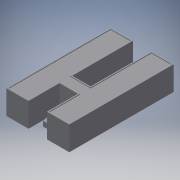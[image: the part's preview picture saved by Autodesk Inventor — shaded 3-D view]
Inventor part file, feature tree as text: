
AUTODESK INVENTOR PART (.ipt)
format: ipt  version: 2018.3 (Build 223284000, 284)  size: 178,688 bytes
history: native  units: mm
features: extrude x6, sketch x6
ambient origin geometry x8: Origin, YZ Plane, XZ Plane, XY Plane, X Axis, Y Axis, Z Axis, Center Point
bodies: Solid1 (feature_tree)
feature tree (12):
  extrude  "Extrusion1"  Depth=19.2mm
  extrude  "Extrusion2"  Depth=15.87mm
  extrude  "Extrusion3"  Depth=26.67mm
  extrude  "Extrusion4"  Depth=6.9mm
  extrude  "Extrusion5"  Depth=27.15mm TaperAngle=0.0deg
  extrude  "Extrusion6"  Depth=0.62mm
  sketch  "Sketch1"  dims[d0=90.0mm d1=19.2mm]
  sketch  "Sketch2"  dims[d2=52.35mm d3=15.87mm]
  sketch  "Sketch3"  dims[d4=19.2mm d5=26.67mm]
  sketch  "Sketch4"  dims[d6=20.67mm d7=0.0mm d8=6.9mm]
  sketch  "Sketch5"  dims[d9=4.29mm d10=27.15mm d11=0.0mm]
  sketch  "Sketch6"  dims[d12=24.88mm d13=14.549065mm d14=2.877mm d15=4.29mm d16=0.0mm d17=6.9mm d18=4.29mm d19=4.48mm d20=18.76mm d21=0.0mm d22=16.68mm d23=1.61mm d24=2.877mm d25=4.29mm d26=0.0mm d27=88.14mm d28=17.34mm d29=52.35mm d30=17.73mm d31=52.35mm d32=17.34mm d33=88.14mm d34=26.67mm d35=0.62mm d36=0.0mm]
